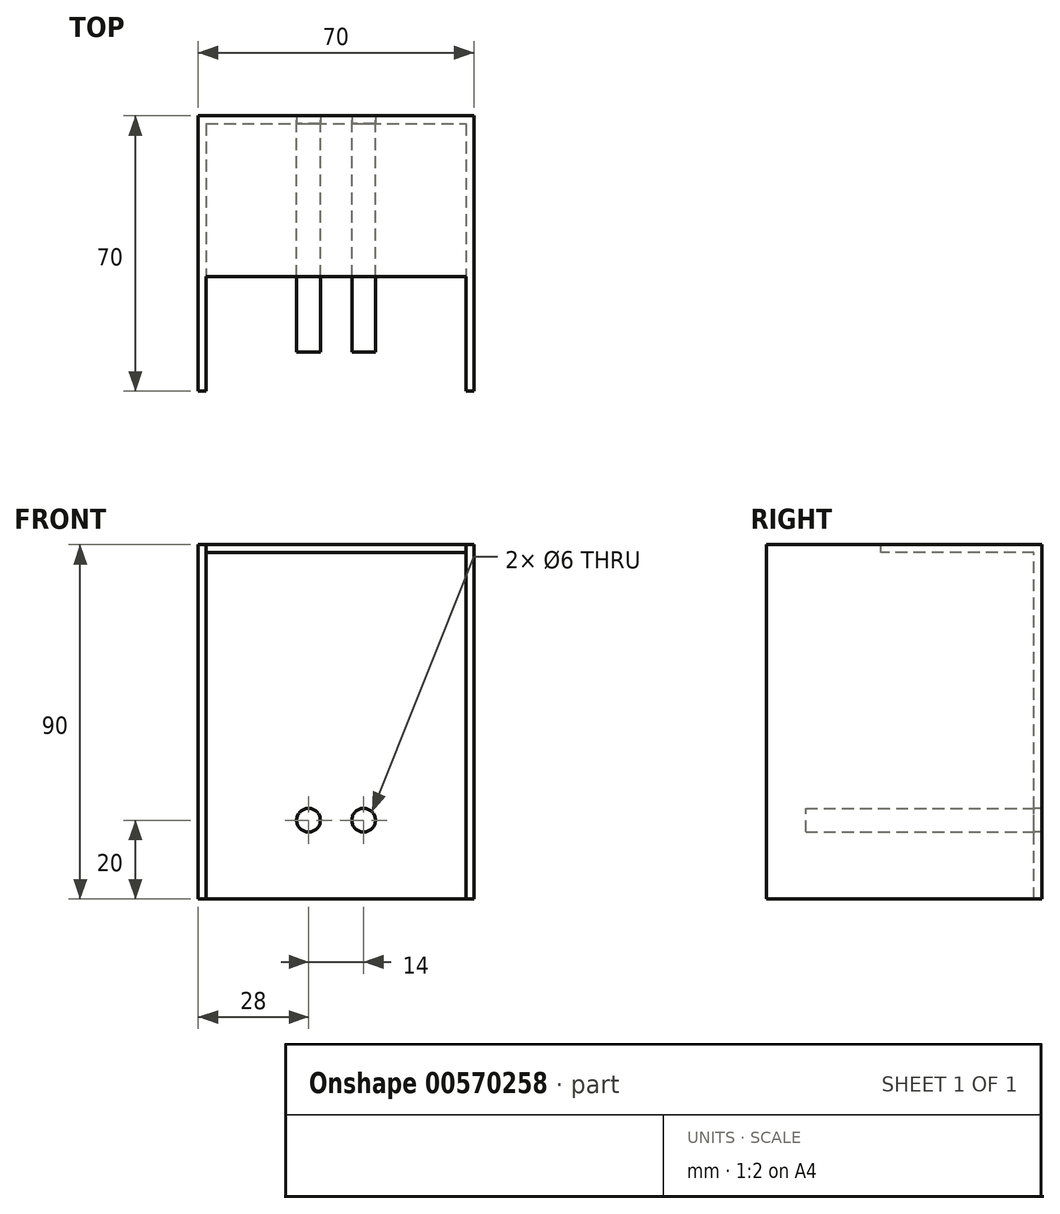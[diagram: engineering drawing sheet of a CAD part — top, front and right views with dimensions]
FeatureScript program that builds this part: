
annotation { "Feature Type Name" : "Feature", "Feature Type Description" : "" }
export const myFeature = defineFeature(function(context is Context, id is Id, definition is map)
    precondition{}
    {
        {
            var Q0;
            Q0=qCreatedBy(makeId("Front.planeOp"),FACE);
            var sketch = newSketch(context, id + "F0", { "sketchPlane" : qUnion([Q0])});
            skLineSegment(sketch, "E0.bottom", {"start": v(0, 0) * mm, "end": v(70, 0) * mm});
            skLineSegment(sketch, "E0.top", {"start": v(0, 90) * mm, "end": v(70, 90) * mm});
            skLineSegment(sketch, "E0.left", {"start": v(0, 0) * mm, "end": v(0, 90) * mm});
            skLineSegment(sketch, "E0.right", {"start": v(70, 0) * mm, "end": v(70, 90) * mm});
            skCircle(sketch, "E1", {"center": v(42, 20) * mm, "radius": 3 * mm});
            skCircle(sketch, "E2", {"center": v(28, 20) * mm, "radius": 3 * mm});
            skSolve(sketch);
        }
        {
            var Q0;
            Q0 = qSketchRegion(id + "F0", true);
            extrude(context, id + "F1", {"entities" : qUnion([Q0]), "oppositeDirection" : true, "depth" : 2 * mm, "offsetDistance" : 25 * mm});
        }
        {
            var Q0;
            Q0=makeQuery(id+"F1.opExtrude","SWEPT_FACE",FACE,{"disambiguationData":[OSD([sQuery(id+"F0.wireOp",EDGE,"E0.left")])]});
            var sketch = newSketch(context, id + "F2", { "sketchPlane" : qUnion([Q0])});
            skLineSegment(sketch, "E3.bottom", {"start": v(0, 0) * mm, "end": v(68, 0) * mm});
            skLineSegment(sketch, "E3.top", {"start": v(0, 90) * mm, "end": v(68, 90) * mm});
            skLineSegment(sketch, "E3.left", {"start": v(0, 0) * mm, "end": v(0, 90) * mm});
            skLineSegment(sketch, "E3.right", {"start": v(68, 0) * mm, "end": v(68, 90) * mm});
            skSolve(sketch);
        }
        {
            var Q0;
            Q0 = qSketchRegion(id + "F2", true);
            extrude(context, id + "F3", {"entities" : qUnion([Q0]), "operationType" : NewBodyOperationType.ADD, "oppositeDirection" : true, "depth" : 2 * mm, "offsetDistance" : 25 * mm});
        }
        {
            var Q0;
            Q0=makeQuery(id+"F1.opExtrude","SWEPT_FACE",FACE,{"disambiguationData":[OSD([sQuery(id+"F0.wireOp",EDGE,"E0.right")])]});
            var sketch = newSketch(context, id + "F4", { "sketchPlane" : qUnion([Q0])});
            skLineSegment(sketch, "E4.bottom", {"start": v(0, 0) * mm, "end": v(-68, 0) * mm});
            skLineSegment(sketch, "E4.top", {"start": v(0, 90) * mm, "end": v(-68, 90) * mm});
            skLineSegment(sketch, "E4.left", {"start": v(0, 0) * mm, "end": v(0, 90) * mm});
            skLineSegment(sketch, "E4.right", {"start": v(-68, 0) * mm, "end": v(-68, 90) * mm});
            skSolve(sketch);
        }
        {
            var Q0;
            Q0 = qSketchRegion(id + "F4", true);
            extrude(context, id + "F5", {"entities" : qUnion([Q0]), "operationType" : NewBodyOperationType.ADD, "oppositeDirection" : true, "depth" : 2 * mm, "offsetDistance" : 25 * mm});
        }
        {
            var Q0;
            Q0=makeQuery(id+"F5.boolean.opBoolean","MERGE",FACE,{"derivedFrom":[makeQuery(id+"F3.boolean.opBoolean","MERGE",FACE,{"derivedFrom":[makeQuery(id+"F1.opExtrude","SWEPT_FACE",FACE,{"disambiguationData":[OSD([sQuery(id+"F0.wireOp",EDGE,"E0.top")])]}),makeQuery(id+"F3.opExtrude","SWEPT_FACE",FACE,{"disambiguationData":[OSD([sQuery(id+"F2.wireOp",EDGE,"E3.top")])]})]}),makeQuery(id+"F5.opExtrude","SWEPT_FACE",FACE,{"disambiguationData":[OSD([sQuery(id+"F4.wireOp",EDGE,"E4.top")])]})]});
            var sketch = newSketch(context, id + "F6", { "sketchPlane" : qUnion([Q0])});
            skLineSegment(sketch, "E5.bottom", {"start": v(2, 0) * mm, "end": v(68, 0) * mm});
            skLineSegment(sketch, "E5.top", {"start": v(2, -38.93) * mm, "end": v(68, -38.93) * mm});
            skLineSegment(sketch, "E5.left", {"start": v(2, 0) * mm, "end": v(2, -38.93) * mm});
            skLineSegment(sketch, "E5.right", {"start": v(68, 0) * mm, "end": v(68, -38.93) * mm});
            skSolve(sketch);
        }
        {
            var Q0;
            Q0 = qSketchRegion(id + "F6", true);
            extrude(context, id + "F7", {"entities" : qUnion([Q0]), "operationType" : NewBodyOperationType.ADD, "oppositeDirection" : true, "depth" : 2 * mm, "offsetDistance" : 25 * mm});
        }
        {
            var Q0;
            Q0=makeQuery(id+"F1.opExtrude","CAP_FACE",FACE,{"disambiguationData":[OSD([sQuery(id+"F0.wireOp",EDGE,"E0.bottom"),sQuery(id+"F0.wireOp",EDGE,"E0.top"),sQuery(id+"F0.wireOp",EDGE,"E0.left"),sQuery(id+"F0.wireOp",EDGE,"E0.right"),sQuery(id+"F0.wireOp",EDGE,"E1"),sQuery(id+"F0.wireOp",EDGE,"E2")])],"isStart":false});
            var sketch = newSketch(context, id + "F8", { "sketchPlane" : qUnion([Q0])});
            skCircle(sketch, "E6", {"center": v(-42, 20) * mm, "radius": 3 * mm});
            skCircle(sketch, "E7", {"center": v(-28, 20) * mm, "radius": 3 * mm});
            skSolve(sketch);
        }
        {
            var Q0;
            Q0 = qSketchRegion(id + "F8", true);
            extrude(context, id + "F9", {"entities" : qUnion([Q0]), "oppositeDirection" : true, "depth" : 60 * mm, "offsetDistance" : 25 * mm});
        }
    });
